# Revit family: Grohe_PlumbingFixtures_ConcealedBody_Eurosmart_36322001a
name_source: partatom
category: Plumbing Fixtures
revit_build: Autodesk Revit 2017 (Build: 20190508_0315(x64)
units: mm (PartAtom-declared; Revit-internal decimal feet)

## family parameters
Cut with Voids When Loaded = No
Host = Face
OmniClass Number = 23.65.00.00
OmniClass Title = Supply and Distribution of Liquids and Gases
Part Type = Normal
Room Calculation Point = No
Round Connector Dimension = Use Diameter
Shared = No

## types (1)
- 36322001
    ADACompliant = No
    Assembly Code = C1030
    AssetType = Fixed
    BIMObjectName = Grohe_PlumbingFixtures_ConcealedBody_Eurosmart_36322001
    CW Connection = Yes
    CWFU = 4.5
    ClassificationName = Uniclass2015
    ClassificationValue = Pr_40_20_87_80
    ColdWaterConnectionDiameter = 10 mm  [stored 0.0328084 ft]
    Color = Blue
    Cost = 0 $
    Default Elevation = 0 mm  [stored 0 ft]
    Description = wall installation. suitable for self-closing final installation sets. with adhesive flange for sealing the wall. 2 stop valves. housing with mixing device. non-return valve. for use with 36 321 000. allows for waterproofing of wall construction surrounding the concealed body. with sealing sleeve.
    DocumentationCertificates = https://www.grohe.com
    DocumentationInstallationGuide = https://www.grohe.com
    DocumentationLiterature = https://www.grohe.com
    DocumentationMaintenance = https://www.grohe.com
    DocumentationTechnical = https://www.grohe.com
    DurationUnit = Years
    Ecojoy = No
    ExpectedLife = 0
    FaucetMaterial = Plastic, Opaque Dark Blue
    Features = wall installation. suitable for self-closing final installation sets. with adhesive flange for sealing the wall. 2 stop valves. housing with mixing device. non-return valve. for use with 36 321 000. allows for waterproofing of wall construction surrounding the concealed body. with sealing sleeve.
    HW Connection = Yes
    HWFU = 4.5
    HotWaterConnectionDiameter = 10 mm  [stored 0.0328084 ft]
    IfcExportAs = IfcPipeFitting
    IfcExportType = IfcPipeFittingType
    Keynote = N13
    LowEmittingMaterial = No
    Manufacturer = Grohe
    ManufacturerName = Grohe
    MasterformatNumber = 01 52 19
    MasterformatTitle = Sanitary Facilities
    Model = Eurosmart Cosmopolitan T Concealed mounting box with mixture
    ModelNumber = 36322001
    ModelReference = Eurosmart Cosmopolitan T Concealed mounting box with mixture
    NBSDescription = Shower thermostatic valves
    NBSObjectName = Grohe - Shower thermostatic valves
    NBSReference = 45-35-70/335
    NominalDepth = 0 mm  [stored 0 ft]
    NominalHeight = 0 mm  [stored 0 ft]
    NominalLength = 0 mm  [stored 0 ft]
    ProductionYear = 2020
    Type Comments = 36322001
    TypeName = 36322001
    URL = https://www.grohe.com
    Vent Connection = No
    WarrantyDurationLabor = 0
    WarrantyDurationParts = 0
    WarrantyDurationUnit = Years
    Waste Connection = No
    _BSBibleVersion = 15
    _BimSpecGuid = 0
    _CurrentRevision = 1
    _DistributedBy = www.bimstore.co

note: [stored X ft] marks values corroborated as IEEE doubles in the binary element streams (Revit-internal decimal feet)

## geometry (parser evidence)
native form markers: Blend x6, Sweep x4
no freeform markers — native parametric forms only
